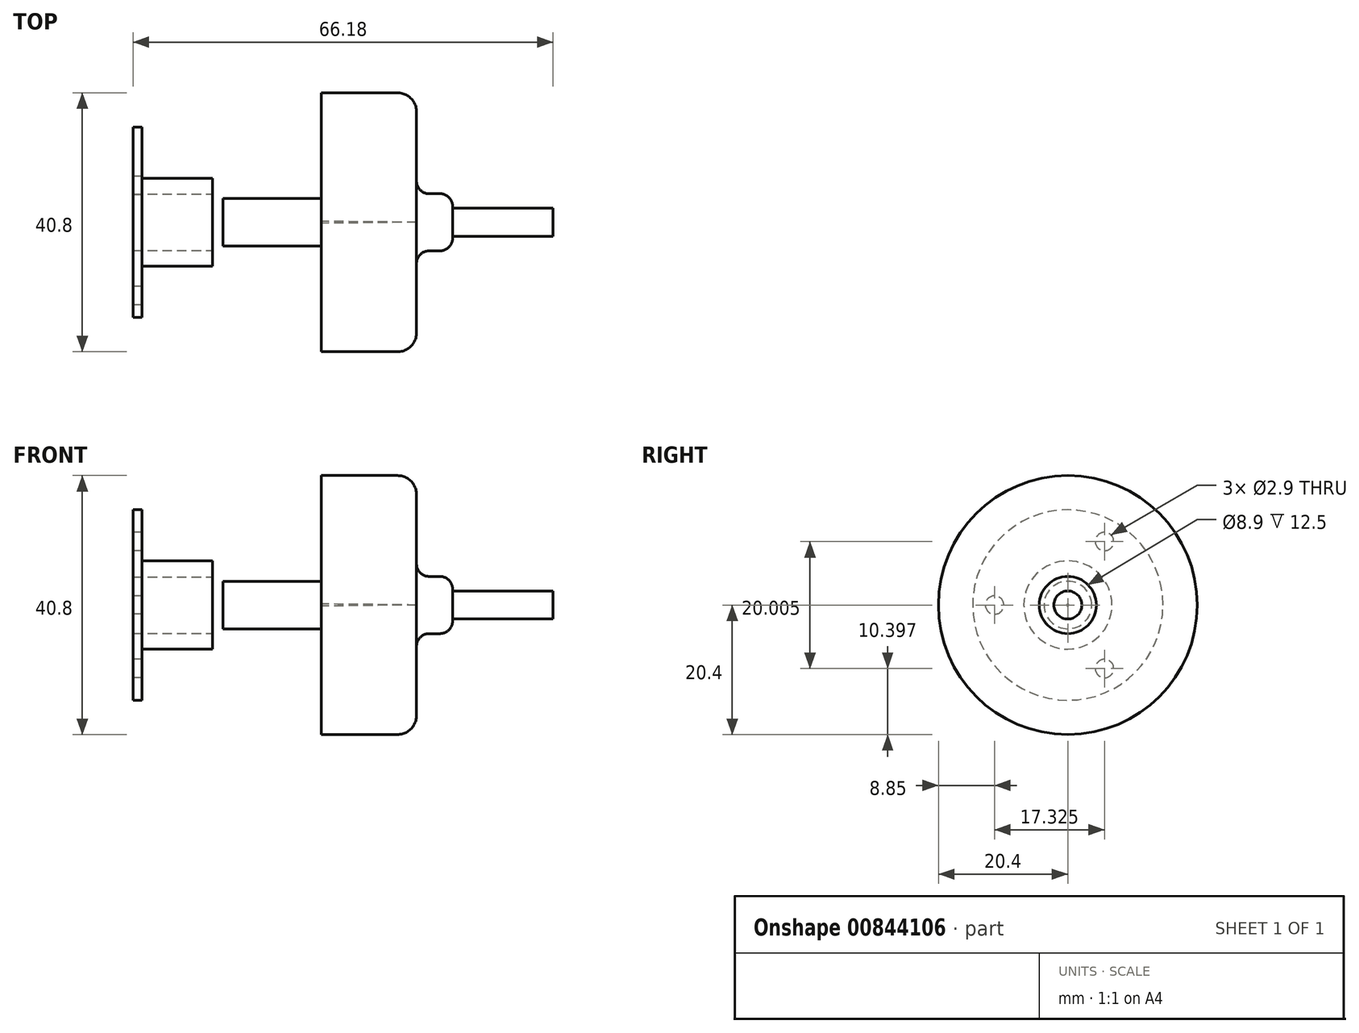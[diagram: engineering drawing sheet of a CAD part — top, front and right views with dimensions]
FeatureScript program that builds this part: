
annotation { "Feature Type Name" : "Feature", "Feature Type Description" : "" }
export const myFeature = defineFeature(function(context is Context, id is Id, definition is map)
    precondition{}
    {
        {
            var Q0;
            Q0=qCreatedBy(makeId("Front.planeOp"),FACE);
            var sketch = newSketch(context, id + "F0", { "sketchPlane" : qUnion([Q0])});
            skLineSegment(sketch, "E0.bottom", {"start": v(-3.93, 20.4) * mm, "end": v(8.07, 20.4) * mm});
            skLineSegment(sketch, "E0.left", {"start": v(-3.93, 20.4) * mm, "end": v(-3.93, 0.16) * mm});
            skLineSegment(sketch, "E1.bottom", {"start": v(13.07, 4.5) * mm, "end": v(14.77, 4.5) * mm});
            skLineSegment(sketch, "E1.top", {"start": v(11.07, 0) * mm, "end": v(16.77, 0) * mm});
            skLineSegment(sketch, "E1.right", {"start": v(16.77, 2.5) * mm, "end": v(16.77, 0) * mm});
            skPoint(sketch, "E2.visualSharp", {"position": v(11.07, 20.4) * mm});
            skArc(sketch, "E2.filletArc", {"start": v(11.07, 17.4) * mm, "mid": v(10.2, 19.52) * mm, "end": v(8.07, 20.4) * mm});
            skPoint(sketch, "E3.orphan", {"position": v(16.77, 0) * mm});
            skPoint(sketch, "E4.orphan", {"position": v(16.77, 2.25) * mm});
            skPoint(sketch, "E5.orphan", {"position": v(-3.93, 0.04) * mm});
            skLineSegment(sketch, "E6", {"start": v(-3.93, 0.16) * mm, "end": v(11.07, 0) * mm});
            skLineSegment(sketch, "E7", {"start": v(11.07, 6.5) * mm, "end": v(11.07, 17.4) * mm});
            skPoint(sketch, "E8.visualSharp", {"position": v(11.07, 4.5) * mm});
            skArc(sketch, "E8.filletArc", {"start": v(11.07, 6.5) * mm, "mid": v(11.66, 5.09) * mm, "end": v(13.07, 4.5) * mm});
            skPoint(sketch, "E9.visualSharp", {"position": v(16.77, 4.5) * mm});
            skArc(sketch, "E9.filletArc", {"start": v(16.77, 2.5) * mm, "mid": v(16.19, 3.91) * mm, "end": v(14.77, 4.5) * mm});
            skLineSegment(sketch, "E10.bottom", {"start": v(-3.93, 3.75) * mm, "end": v(-19.42, 3.75) * mm});
            skLineSegment(sketch, "E10.top", {"start": v(-3.93, 0) * mm, "end": v(-19.42, 0) * mm});
            skLineSegment(sketch, "E10.left", {"start": v(-3.93, 3.75) * mm, "end": v(-3.93, 0) * mm});
            skLineSegment(sketch, "E10.right", {"start": v(-19.42, 3.75) * mm, "end": v(-19.42, 0) * mm});
            skLineSegment(sketch, "E11.bottom", {"start": v(16.77, 0) * mm, "end": v(32.6, 0) * mm});
            skLineSegment(sketch, "E11.top", {"start": v(16.77, 2.21) * mm, "end": v(32.6, 2.21) * mm});
            skLineSegment(sketch, "E11.left", {"start": v(16.77, 0) * mm, "end": v(16.77, 2.21) * mm});
            skLineSegment(sketch, "E11.right", {"start": v(32.6, 0) * mm, "end": v(32.6, 2.21) * mm});
            skSolve(sketch);
        }
        {
            var Q0;
            Q0=makeQuery(id+"F0.imprint","IMPRINT",FACE,{"disambiguationData":[TD([[makeQuery(id+"F0.imprint","IMPRINT",EDGE,{"derivedFrom":sQuery(id+"F0.wireOp",EDGE,"E0.bottom")}),-1.0]])]});
            var Q1;
            {var subQ3=sQuery(id+"F0.wireOp",EDGE,"E10.bottom");Q1=makeQuery(id+"F0.imprint","IMPRINT",FACE,{"disambiguationData":[TD([[makeQuery(id+"F0.imprint","IMPRINT",EDGE,{"derivedFrom":subQ3}),1.0]])]});}
            var Q2;
            Q2=makeQuery(id+"F0.imprint","IMPRINT",FACE,{"disambiguationData":[TD([[makeQuery(id+"F0.imprint","IMPRINT",EDGE,{"derivedFrom":sQuery(id+"F0.wireOp",EDGE,"E11.bottom")}),1.0]])]});
            var Q3;
            Q3=sQuery(id+"F0.wireOp",EDGE,"E10.top");
            revolve(context, id + "F1", {"surfaceOperationType" : NewSurfaceOperationType.NEW, "entities" : qUnion([Q0, Q1, Q2]), "axis" : qUnion([Q3]), "revolveType" : RevolveType.FULL});
        }
        {
            var Q0;
            Q0=qCreatedBy(makeId("Front.planeOp"),FACE);
            var sketch = newSketch(context, id + "F2", { "sketchPlane" : qUnion([Q0])});
            skLineSegment(sketch, "E12.bottom", {"start": v(-33.58, 15) * mm, "end": v(-32.18, 15) * mm});
            skLineSegment(sketch, "E12.top", {"start": v(-33.58, 0) * mm, "end": v(-32.18, 0) * mm});
            skLineSegment(sketch, "E12.left", {"start": v(-33.58, 15) * mm, "end": v(-33.58, 0) * mm});
            skLineSegment(sketch, "E12.right", {"start": v(-32.18, 15) * mm, "end": v(-32.18, 0) * mm});
            skLineSegment(sketch, "E13.bottom", {"start": v(-32.18, 6.95) * mm, "end": v(-21.08, 6.95) * mm});
            skLineSegment(sketch, "E13.top", {"start": v(-32.18, 0) * mm, "end": v(-21.08, 0) * mm});
            skLineSegment(sketch, "E13.left", {"start": v(-32.18, 6.95) * mm, "end": v(-32.18, 0) * mm});
            skLineSegment(sketch, "E13.right", {"start": v(-21.08, 6.95) * mm, "end": v(-21.08, 0) * mm});
            skSolve(sketch);
        }
        {
            var Q0;
            Q0=makeQuery(id+"F2.imprint","IMPRINT",FACE,{"disambiguationData":[TD([[makeQuery(id+"F2.imprint","IMPRINT",EDGE,{"derivedFrom":sQuery(id+"F2.wireOp",EDGE,"E13.bottom")}),-1.0]])]});
            var Q1;
            Q1=makeQuery(id+"F2.imprint","IMPRINT",FACE,{"disambiguationData":[TD([[makeQuery(id+"F2.imprint","IMPRINT",EDGE,{"derivedFrom":sQuery(id+"F2.wireOp",EDGE,"E12.bottom")}),-1.0]])]});
            var Q2;
            Q2=sQuery(id+"F2.wireOp",EDGE,"E13.top");
            revolve(context, id + "F3", {"surfaceOperationType" : NewSurfaceOperationType.NEW, "entities" : qUnion([Q0, Q1]), "axis" : qUnion([Q2]), "revolveType" : RevolveType.FULL});
        }
        {
            var Q0;
            Q0=makeQuery(id+"F3.opRevolve","SWEPT_FACE",FACE,{"disambiguationData":[OSD([sQuery(id+"F2.wireOp",EDGE,"E13.right")])]});
            var sketch = newSketch(context, id + "F4", { "sketchPlane" : qUnion([Q0])});
            skCircle(sketch, "E14", {"center": v(0, 0) * mm, "radius": 4.45 * mm});
            skSolve(sketch);
        }
        {
            var Q0;
            Q0=makeQuery(id+"F4.imprint","IMPRINT",FACE,{"disambiguationData":[TD([[makeQuery(id+"F4.imprint","IMPRINT",EDGE,{"derivedFrom":sQuery(id+"F4.wireOp",EDGE,"E14")}),1.0]])]});
            extrude(context, id + "F5", {"entities" : qUnion([Q0]), "operationType" : NewBodyOperationType.REMOVE, "oppositeDirection" : true, "depth" : 25 * mm, "offsetDistance" : 25 * mm});
        }
        {
            var Q0;
            Q0=makeQuery(id+"F3.opRevolve","SWEPT_FACE",FACE,{"disambiguationData":[OSD([sQuery(id+"F2.wireOp",EDGE,"E12.left")])]});
            var sketch = newSketch(context, id + "F6", { "sketchPlane" : qUnion([Q0])});
            skCircle(sketch, "E15", {"center": v(0, 0) * mm, "radius": 11.55 * mm, "construction": true});
            skCircle(sketch, "E16", {"center": v(11.55, 0) * mm, "radius": 1.45 * mm});
            skCircle(sketch, "E17.1.0", {"center": v(-5.77, 10) * mm, "radius": 1.45 * mm});
            skCircle(sketch, "E17.2.0", {"center": v(-5.78, -10) * mm, "radius": 1.45 * mm});
            skSolve(sketch);
        }
        {
            var Q0;
            Q0=makeQuery(id+"F6.imprint","IMPRINT",FACE,{"disambiguationData":[TD([[makeQuery(id+"F6.imprint","IMPRINT",EDGE,{"derivedFrom":sQuery(id+"F6.wireOp",EDGE,"E17.1.0")}),1.0]])]});
            var Q1;
            Q1=makeQuery(id+"F6.imprint","IMPRINT",FACE,{"disambiguationData":[TD([[makeQuery(id+"F6.imprint","IMPRINT",EDGE,{"derivedFrom":sQuery(id+"F6.wireOp",EDGE,"E16")}),1.0]])]});
            var Q2;
            Q2=makeQuery(id+"F6.imprint","IMPRINT",FACE,{"disambiguationData":[TD([[makeQuery(id+"F6.imprint","IMPRINT",EDGE,{"derivedFrom":sQuery(id+"F6.wireOp",EDGE,"E17.2.0")}),1.0]])]});
            extrude(context, id + "F7", {"entities" : qUnion([Q0, Q1, Q2]), "operationType" : NewBodyOperationType.REMOVE, "oppositeDirection" : true, "depth" : 2 * mm, "offsetDistance" : 25 * mm});
        }
    });
